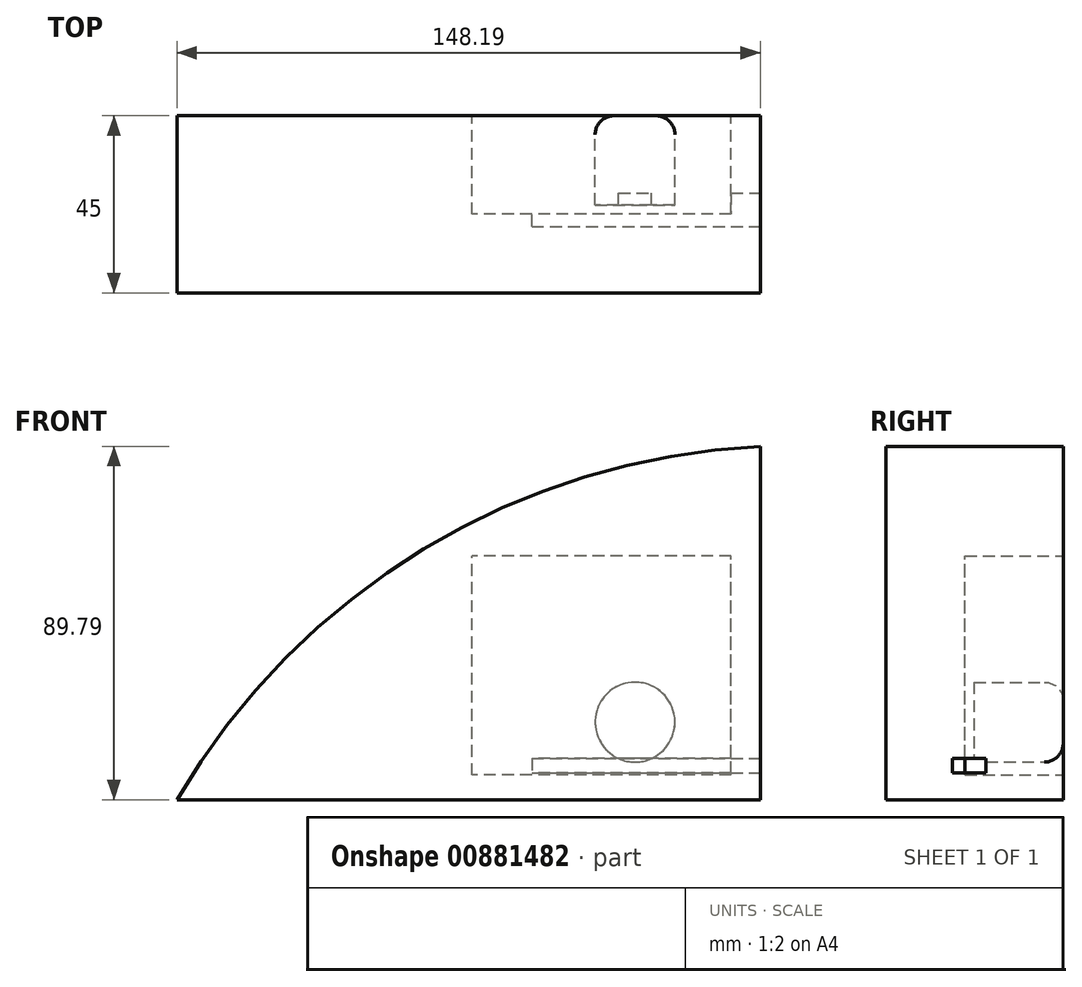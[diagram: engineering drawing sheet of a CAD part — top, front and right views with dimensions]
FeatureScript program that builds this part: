
annotation { "Feature Type Name" : "Feature", "Feature Type Description" : "" }
export const myFeature = defineFeature(function(context is Context, id is Id, definition is map)
    precondition{}
    {
        {
            var Q0;
            Q0=qCreatedBy(makeId("Front.planeOp"),FACE);
            var sketch = newSketch(context, id + "F0", { "sketchPlane" : qUnion([Q0])});
            skLineSegment(sketch, "E0.bottom", {"start": v(-74.97, 44.9) * mm, "end": v(73.22, 44.9) * mm});
            skLineSegment(sketch, "E0.top", {"start": v(-74.97, -45.1) * mm, "end": v(73.22, -45.1) * mm});
            skLineSegment(sketch, "E0.left", {"start": v(-74.97, 44.9) * mm, "end": v(-74.97, -45.1) * mm});
            skLineSegment(sketch, "E0.right", {"start": v(73.22, 44.9) * mm, "end": v(73.22, -45.1) * mm});
            skSolve(sketch);
        }
        {
            var Q0;
            Q0=makeQuery(id+"F0.imprint","IMPRINT",FACE,{"disambiguationData":[TD([[makeQuery(id+"F0.imprint","IMPRINT",EDGE,{"derivedFrom":sQuery(id+"F0.wireOp",EDGE,"E0.bottom")}),-1.0]])]});
            extrude(context, id + "F1", {"entities" : qUnion([Q0]), "depth" : 45 * mm, "offsetDistance" : 25 * mm});
        }
        {
            var Q0;
            Q0=makeQuery(id+"F1.opExtrude","SWEPT_EDGE",EDGE,{"disambiguationData":[OSD([sQuery(id+"F0.wireOp",EDGE,"E0.bottom"),sQuery(id+"F0.wireOp",EDGE,"E0.left")])]});
            fillet(context, id + "F2", {"entities" : qUnion([Q0]), "radius" : 181.8 * mm, "tangentPropagation" : true, "allowEdgeOverflow" : false});
        }
        {
            var Q0;
            Q0=makeQuery(id+"F1.opExtrude","CAP_FACE",FACE,{"disambiguationData":[OSD([sQuery(id+"F0.wireOp",EDGE,"E0.bottom"),sQuery(id+"F0.wireOp",EDGE,"E0.top"),sQuery(id+"F0.wireOp",EDGE,"E0.left"),sQuery(id+"F0.wireOp",EDGE,"E0.right")])],"isStart":true});
            var sketch = newSketch(context, id + "F3", { "sketchPlane" : qUnion([Q0])});
            skLineSegment(sketch, "E1.bottom", {"start": v(-65.83, -38.81) * mm, "end": v(0, -38.81) * mm});
            skLineSegment(sketch, "E1.top", {"start": v(-65.83, 16.87) * mm, "end": v(0, 16.87) * mm});
            skLineSegment(sketch, "E1.left", {"start": v(-65.83, -38.81) * mm, "end": v(-65.83, 16.87) * mm});
            skLineSegment(sketch, "E1.right", {"start": v(0, -38.81) * mm, "end": v(0, 16.87) * mm});
            skSolve(sketch);
        }
        {
            var Q0;
            Q0=makeQuery(id+"F3.imprint","IMPRINT",FACE,{"disambiguationData":[TD([[makeQuery(id+"F3.imprint","IMPRINT",EDGE,{"derivedFrom":sQuery(id+"F3.wireOp",EDGE,"E1.bottom")}),1.0]])]});
            extrude(context, id + "F4", {"entities" : qUnion([Q0]), "operationType" : NewBodyOperationType.REMOVE, "oppositeDirection" : true, "depth" : 25 * mm, "offsetDistance" : 25 * mm});
        }
        {
            var Q0;
            Q0=makeQuery(id+"F3.imprint","IMPRINT",FACE,{"disambiguationData":[TD([[makeQuery(id+"F3.imprint","IMPRINT",EDGE,{"derivedFrom":sQuery(id+"F3.wireOp",EDGE,"E1.bottom")}),1.0]])]});
            var sketch = newSketch(context, id + "F5", { "sketchPlane" : qUnion([Q0])});
            skCircle(sketch, "E2", {"center": v(-41.41, -25.37) * mm, "radius": 10.15 * mm});
            skSolve(sketch);
        }
        {
            var Q0;
            Q0=makeQuery(id+"F5.imprint","IMPRINT",FACE,{"disambiguationData":[TD([[makeQuery(id+"F5.imprint","IMPRINT",EDGE,{"derivedFrom":sQuery(id+"F5.wireOp",EDGE,"E2")}),1.0]])]});
            extrude(context, id + "F6", {"entities" : qUnion([Q0]), "oppositeDirection" : true, "depth" : 22.7 * mm, "offsetDistance" : 25 * mm});
        }
        {
            var Q0;
            Q0=makeQuery(id+"F6.opExtrude","CAP_EDGE",EDGE,{"disambiguationData":[OSD([sQuery(id+"F5.wireOp",EDGE,"E2")])],"isStart":true});
            fillet(context, id + "F7", {"entities" : qUnion([Q0]), "radius" : 4.83 * mm, "tangentPropagation" : true, "allowEdgeOverflow" : false});
        }
        {
            var Q0;
            Q0=makeQuery(id+"F1.opExtrude","SWEPT_FACE",FACE,{"disambiguationData":[OSD([sQuery(id+"F0.wireOp",EDGE,"E0.right")])]});
            var sketch = newSketch(context, id + "F8", { "sketchPlane" : qUnion([Q0])});
            skLineSegment(sketch, "E3.bottom", {"start": v(-28.14, -34.62) * mm, "end": v(-19.63, -34.62) * mm});
            skLineSegment(sketch, "E3.top", {"start": v(-28.14, -38.3) * mm, "end": v(-19.63, -38.3) * mm});
            skLineSegment(sketch, "E3.left", {"start": v(-28.14, -34.62) * mm, "end": v(-28.14, -38.3) * mm});
            skLineSegment(sketch, "E3.right", {"start": v(-19.63, -34.62) * mm, "end": v(-19.63, -38.3) * mm});
            skSolve(sketch);
        }
        {
            var Q0;
            Q0=makeQuery(id+"F8.imprint","IMPRINT",FACE,{"disambiguationData":[TD([[makeQuery(id+"F8.imprint","IMPRINT",EDGE,{"derivedFrom":sQuery(id+"F8.wireOp",EDGE,"E3.bottom")}),-1.0]])]});
            extrude(context, id + "F9", {"entities" : qUnion([Q0]), "operationType" : NewBodyOperationType.REMOVE, "oppositeDirection" : true, "depth" : 58 * mm, "offsetDistance" : 25 * mm});
        }
    });
